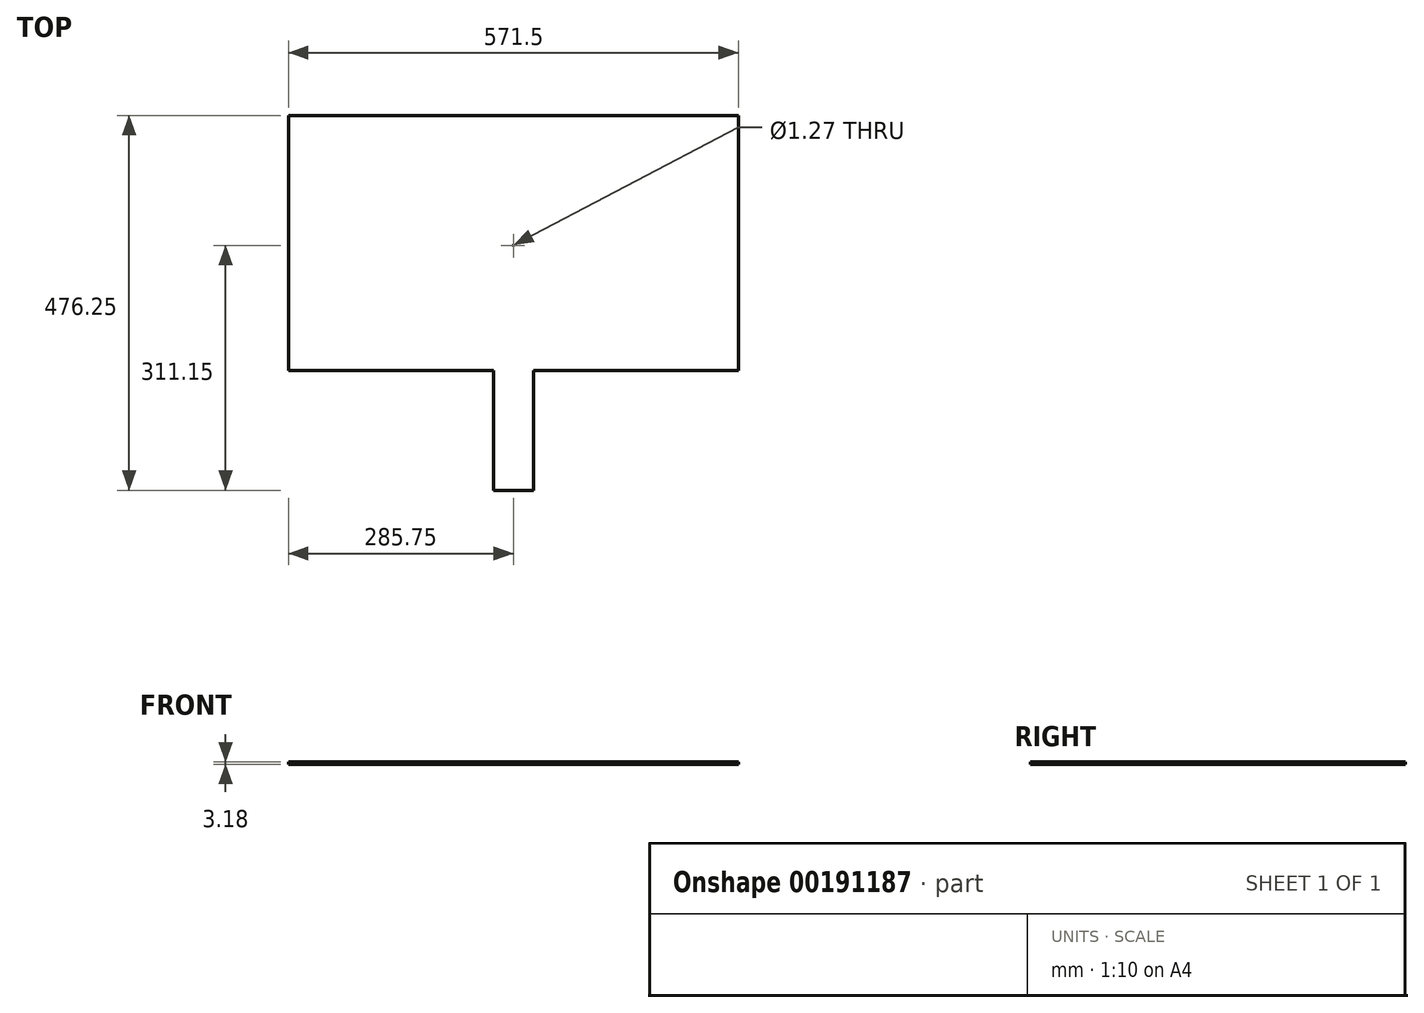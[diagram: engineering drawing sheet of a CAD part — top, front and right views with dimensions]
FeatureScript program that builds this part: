
annotation { "Feature Type Name" : "Feature", "Feature Type Description" : "" }
export const myFeature = defineFeature(function(context is Context, id is Id, definition is map)
    precondition{}
    {
        {
            var Q0;
            Q0=qCreatedBy(makeId("Top.planeOp"),FACE);
            var sketch = newSketch(context, id + "F0", { "sketchPlane" : qUnion([Q0])});
            skLineSegment(sketch, "E0", {"start": v(0, -635.05) * mm, "end": v(0, -914.35) * mm, "construction": true});
            skLineSegment(sketch, "E1.bottom", {"start": v(285.75, -298.45) * mm, "end": v(-285.75, -298.45) * mm, "construction": true});
            skLineSegment(sketch, "E1.top", {"start": v(285.75, 298.45) * mm, "end": v(-285.75, 298.45) * mm, "construction": true});
            skLineSegment(sketch, "E1.left", {"start": v(285.75, -298.45) * mm, "end": v(285.75, 298.45) * mm, "construction": true});
            skLineSegment(sketch, "E1.right", {"start": v(-285.75, -298.45) * mm, "end": v(-285.75, 298.45) * mm, "construction": true});
            skPoint(sketch, "E1.middle", {"position": v(0, 0) * mm});
            skLineSegment(sketch, "E2", {"start": v(-842.63, 0) * mm, "end": v(1673.01, 0) * mm, "construction": true});
            skPoint(sketch, "E2.endSnap0", {"position": v(285.75, 0) * mm});
            skLineSegment(sketch, "E3", {"start": v(323.85, 298.45) * mm, "end": v(323.85, -298.45) * mm, "construction": true});
            skLineSegment(sketch, "E4", {"start": v(323.85, -298.45) * mm, "end": v(577.85, -298.45) * mm});
            skLineSegment(sketch, "E5", {"start": v(577.85, -298.45) * mm, "end": v(577.85, 298.45) * mm, "construction": true});
            skLineSegment(sketch, "E6.bottom", {"start": v(-323.85, 298.45) * mm, "end": v(-577.85, 298.45) * mm});
            skLineSegment(sketch, "E6.top", {"start": v(-323.85, -298.45) * mm, "end": v(-577.85, -298.45) * mm});
            skLineSegment(sketch, "E6.left", {"start": v(-323.85, 298.45) * mm, "end": v(-323.85, -298.45) * mm, "construction": true});
            skLineSegment(sketch, "E6.right", {"start": v(-577.85, 298.45) * mm, "end": v(-577.85, -298.45) * mm});
            skLineSegment(sketch, "E7.bottom", {"start": v(285.75, 298.45) * mm, "end": v(1187.45, 298.45) * mm});
            skLineSegment(sketch, "E7.top", {"start": v(615.95, -298.45) * mm, "end": v(1187.45, -298.45) * mm});
            skLineSegment(sketch, "E7.left", {"start": v(615.95, 298.45) * mm, "end": v(615.95, -298.45) * mm, "construction": true});
            skLineSegment(sketch, "E8.bottom", {"start": v(-285.75, -336.55) * mm, "end": v(285.75, -336.55) * mm, "construction": true});
            skLineSegment(sketch, "E8.top", {"start": v(-285.75, -622.3) * mm, "end": v(-25.4, -622.3) * mm});
            skLineSegment(sketch, "E8.left", {"start": v(-285.75, -336.55) * mm, "end": v(-285.75, -622.3) * mm});
            skLineSegment(sketch, "E8.right", {"start": v(285.75, -336.55) * mm, "end": v(285.75, -622.3) * mm});
            skLineSegment(sketch, "E9.bottom", {"start": v(-285.75, 336.55) * mm, "end": v(285.75, 336.55) * mm, "construction": true});
            skLineSegment(sketch, "E9.left", {"start": v(-285.75, 336.55) * mm, "end": v(-285.75, 349.25) * mm});
            skLineSegment(sketch, "E10", {"start": v(285.75, -298.45) * mm, "end": v(323.85, -298.45) * mm});
            skLineSegment(sketch, "E11", {"start": v(577.85, -298.45) * mm, "end": v(615.95, -298.45) * mm});
            skLineSegment(sketch, "E12", {"start": v(-323.85, -298.45) * mm, "end": v(-285.75, -298.45) * mm});
            skLineSegment(sketch, "E13", {"start": v(-323.85, 298.45) * mm, "end": v(-285.75, 298.45) * mm});
            skLineSegment(sketch, "E14", {"start": v(285.75, -298.45) * mm, "end": v(285.75, -336.55) * mm});
            skLineSegment(sketch, "E15", {"start": v(-285.75, -298.45) * mm, "end": v(-285.75, -336.55) * mm});
            skLineSegment(sketch, "E16.bottom", {"start": v(1187.45, 298.45) * mm, "end": v(1276.35, 298.45) * mm});
            skLineSegment(sketch, "E16.top", {"start": v(1187.45, -298.45) * mm, "end": v(1276.35, -298.45) * mm});
            skLineSegment(sketch, "E16.left", {"start": v(1187.45, 298.45) * mm, "end": v(1187.45, -298.45) * mm, "construction": true});
            skLineSegment(sketch, "E16.right", {"start": v(1276.35, 298.45) * mm, "end": v(1276.35, -298.45) * mm});
            skLineSegment(sketch, "E17.right", {"start": v(361.95, 577.85) * mm, "end": v(361.95, 349.25) * mm});
            skLineSegment(sketch, "E18.top", {"start": v(-285.75, 298.45) * mm, "end": v(-361.95, 298.45) * mm});
            skLineSegment(sketch, "E18.left", {"start": v(-285.75, 704.85) * mm, "end": v(-285.75, 577.85) * mm});
            skLineSegment(sketch, "E18.right", {"start": v(-361.95, 577.85) * mm, "end": v(-361.95, 349.25) * mm});
            skLineSegment(sketch, "E19.top", {"start": v(-285.75, 704.85) * mm, "end": v(285.75, 704.85) * mm});
            skLineSegment(sketch, "E20", {"start": v(-361.95, 349.25) * mm, "end": v(-285.75, 349.25) * mm});
            skLineSegment(sketch, "E21", {"start": v(285.75, 349.25) * mm, "end": v(361.95, 349.25) * mm});
            skLineSegment(sketch, "E22.top", {"start": v(-25.4, -774.7) * mm, "end": v(25.4, -774.7) * mm});
            skLineSegment(sketch, "E22.left", {"start": v(25.4, -622.3) * mm, "end": v(25.4, -774.7) * mm});
            skLineSegment(sketch, "E22.right", {"start": v(-25.4, -622.3) * mm, "end": v(-25.4, -774.7) * mm});
            skLineSegment(sketch, "E23.trimOffspring", {"start": v(25.4, -622.3) * mm, "end": v(285.75, -622.3) * mm});
            skLineSegment(sketch, "E24", {"start": v(361.95, 577.85) * mm, "end": v(285.75, 577.85) * mm});
            skLineSegment(sketch, "E25", {"start": v(-361.95, 577.85) * mm, "end": v(-285.75, 577.85) * mm});
            skLineSegment(sketch, "E26", {"start": v(-285.75, 349.25) * mm, "end": v(-285.75, 298.45) * mm});
            skLineSegment(sketch, "E27", {"start": v(-285.75, 577.85) * mm, "end": v(-285.75, 349.25) * mm, "construction": true});
            skCircle(sketch, "E28", {"center": v(0, 0) * mm, "radius": 0.64 * mm});
            skPoint(sketch, "E29", {"position": v(450.85, 0) * mm});
            skPoint(sketch, "E30", {"position": v(323.85, 0) * mm});
            skPoint(sketch, "E31", {"position": v(577.85, 0) * mm});
            skPoint(sketch, "E32", {"position": v(615.95, 0) * mm});
            skPoint(sketch, "E33", {"position": v(1187.45, 0) * mm});
            skPoint(sketch, "E34", {"position": v(-323.85, 0) * mm});
            skPoint(sketch, "E35", {"position": v(-577.85, 0) * mm});
            skPoint(sketch, "E36", {"position": v(0, -336.55) * mm});
            skPoint(sketch, "E37", {"position": v(0, -590.55) * mm});
            skPoint(sketch, "E38", {"position": v(0, 349.25) * mm});
            skPoint(sketch, "E39", {"position": v(0, 577.85) * mm});
            skPoint(sketch, "E40", {"position": v(0, 463.55) * mm});
            skPoint(sketch, "E41", {"position": v(-450.85, 0) * mm});
            skPoint(sketch, "E42", {"position": v(901.7, 0) * mm});
            skPoint(sketch, "E43", {"position": v(0, -463.55) * mm});
            skCircle(sketch, "E44", {"center": v(-450.85, 0) * mm, "radius": 0.64 * mm});
            skCircle(sketch, "E45", {"center": v(450.85, 0) * mm, "radius": 0.63 * mm});
            skCircle(sketch, "E46", {"center": v(901.7, 0) * mm, "radius": 0.64 * mm});
            skCircle(sketch, "E47", {"center": v(0, -463.55) * mm, "radius": 0.63 * mm});
            skCircle(sketch, "E48", {"center": v(0, 463.55) * mm, "radius": 0.63 * mm});
            skPoint(sketch, "E49", {"position": v(0, -774.7) * mm});
            skLineSegment(sketch, "E50.trimOffspring", {"start": v(177.8, -622.3) * mm, "end": v(285.75, -622.3) * mm});
            skLineSegment(sketch, "E51", {"start": v(285.75, 704.85) * mm, "end": v(285.75, 577.85) * mm});
            skLineSegment(sketch, "E52", {"start": v(-285.75, 590.55) * mm, "end": v(285.75, 590.55) * mm, "construction": true});
            skPoint(sketch, "E53", {"position": v(990.6, 0) * mm});
            skPoint(sketch, "E54", {"position": v(812.8, 0) * mm});
            skCircle(sketch, "E55", {"center": v(812.8, 0) * mm, "radius": 0.64 * mm});
            skCircle(sketch, "E56", {"center": v(990.6, 0) * mm, "radius": 0.64 * mm});
            skLineSegment(sketch, "E57", {"start": v(-285.75, -590.55) * mm, "end": v(285.75, -590.55) * mm, "construction": true});
            skLineSegment(sketch, "E58", {"start": v(-254, -336.55) * mm, "end": v(-254, -590.55) * mm, "construction": true});
            skLineSegment(sketch, "E59.MirrorCS", {"start": v(254, -336.55) * mm, "end": v(254, -590.55) * mm, "construction": true});
            skLineSegment(sketch, "E60", {"start": v(254, -336.55) * mm, "end": v(-254, -590.55) * mm, "construction": true});
            skLineSegment(sketch, "E61", {"start": v(-254, -336.55) * mm, "end": v(254, -590.55) * mm, "construction": true});
            skLineSegment(sketch, "E62", {"start": v(285.75, 298.45) * mm, "end": v(-285.75, -298.45) * mm, "construction": true});
            skLineSegment(sketch, "E63", {"start": v(-285.75, 298.45) * mm, "end": v(285.75, -298.45) * mm, "construction": true});
            skLineSegment(sketch, "E64", {"start": v(-254, 590.55) * mm, "end": v(-254, 336.55) * mm, "construction": true});
            skLineSegment(sketch, "E65.MirrorCS", {"start": v(254, 590.55) * mm, "end": v(254, 336.55) * mm, "construction": true});
            skLineSegment(sketch, "E66", {"start": v(-254, 590.55) * mm, "end": v(254, 336.55) * mm, "construction": true});
            skLineSegment(sketch, "E67", {"start": v(-254, 336.55) * mm, "end": v(254, 590.55) * mm, "construction": true});
            skLineSegment(sketch, "E68", {"start": v(323.85, 298.45) * mm, "end": v(577.85, -298.45) * mm, "construction": true});
            skLineSegment(sketch, "E69", {"start": v(577.85, 298.45) * mm, "end": v(323.85, -298.45) * mm, "construction": true});
            skLineSegment(sketch, "E70", {"start": v(1187.45, 298.45) * mm, "end": v(615.95, -298.45) * mm, "construction": true});
            skLineSegment(sketch, "E71", {"start": v(-323.85, 298.45) * mm, "end": v(-577.85, -298.45) * mm, "construction": true});
            skLineSegment(sketch, "E72", {"start": v(-577.85, 298.45) * mm, "end": v(-323.85, -298.45) * mm, "construction": true});
            skLineSegment(sketch, "E73", {"start": v(615.95, 298.45) * mm, "end": v(1187.45, -298.45) * mm, "construction": true});
            skLineSegment(sketch, "E74", {"start": v(285.75, 298.45) * mm, "end": v(285.75, 349.25) * mm});
            skSolve(sketch);
        }
        {
            var Q0;
            Q0 = qSketchRegion(id + "F0", true);
            extrude(context, id + "F1", {"entities" : qUnion([Q0]), "depth" : 3.17 * mm});
        }
        {
            var Q0;
            Q0=makeQuery(id+"F1.opExtrude","CAP_FACE",FACE,{"disambiguationData":[OSD([sQuery(id+"F0.wireOp",EDGE,"E4"),sQuery(id+"F0.wireOp",EDGE,"mRY2fwng-EMyn-YxYV-NyzR-yqdV6J5uKH8S"),sQuery(id+"F0.wireOp",EDGE,"E6.bottom"),sQuery(id+"F0.wireOp",EDGE,"E6.top"),sQuery(id+"F0.wireOp",EDGE,"E6.right"),sQuery(id+"F0.wireOp",EDGE,"E7.bottom"),sQuery(id+"F0.wireOp",EDGE,"E7.top"),sQuery(id+"F0.wireOp",EDGE,"E8.left"),sQuery(id+"F0.wireOp",EDGE,"E8.right"),sQuery(id+"F0.wireOp",EDGE,"E10"),sQuery(id+"F0.wireOp",EDGE,"sA4iQwFo-DiBT-fMGT-JzR6-p6F9ceSemcnJ"),sQuery(id+"F0.wireOp",EDGE,"E11"),sQuery(id+"F0.wireOp",EDGE,"E12"),sQuery(id+"F0.wireOp",EDGE,"E14"),sQuery(id+"F0.wireOp",EDGE,"E15"),sQuery(id+"F0.wireOp",EDGE,"E16.bottom"),sQuery(id+"F0.wireOp",EDGE,"E16.top"),sQuery(id+"F0.wireOp",EDGE,"E16.right"),sQuery(id+"F0.wireOp",EDGE,"E17.top"),sQuery(id+"F0.wireOp",EDGE,"E17.right"),sQuery(id+"F0.wireOp",EDGE,"E18.top"),sQuery(id+"F0.wireOp",EDGE,"E18.right"),sQuery(id+"F0.wireOp",EDGE,"E19.bottom"),sQuery(id+"F0.wireOp",EDGE,"E19.top"),sQuery(id+"F0.wireOp",EDGE,"E20"),sQuery(id+"F0.wireOp",EDGE,"E21"),sQuery(id+"F0.wireOp",EDGE,"E8.top"),sQuery(id+"F0.wireOp",EDGE,"E22.top"),sQuery(id+"F0.wireOp",EDGE,"E22.left"),sQuery(id+"F0.wireOp",EDGE,"E22.right"),sQuery(id+"F0.wireOp",EDGE,"E23.trimOffspring"),sQuery(id+"F0.wireOp",EDGE,"4iudcIEB-iYir-bAQA-znhg-HSLRRKW8f51n"),sQuery(id+"F0.wireOp",EDGE,"xF0T9dwZ-jTZR-t2eK-ofbr-AFZm1iYlZQ4e"),sQuery(id+"F0.wireOp",EDGE,"E24"),sQuery(id+"F0.wireOp",EDGE,"E25"),sQuery(id+"F0.wireOp",EDGE,"73229018-e269-4e0e-8c85-239f03a1994d"),sQuery(id+"F0.wireOp",EDGE,"6cf454b5-ede0-49d4-9204-e5f682ce5569"),sQuery(id+"F0.wireOp",EDGE,"E26"),sQuery(id+"F0.wireOp",EDGE,"70cc8ee7-993e-4542-805c-fe784006b110.trimOffspring"),sQuery(id+"F0.wireOp",EDGE,"E28"),sQuery(id+"F0.wireOp",EDGE,"E44"),sQuery(id+"F0.wireOp",EDGE,"E45"),sQuery(id+"F0.wireOp",EDGE,"E46"),sQuery(id+"F0.wireOp",EDGE,"E47"),sQuery(id+"F0.wireOp",EDGE,"E48"),sQuery(id+"F0.wireOp",EDGE,"E50.trimOffspring"),sQuery(id+"F0.wireOp",EDGE,"E51")])],"isStart":false});
            var sketch = newSketch(context, id + "F2", { "sketchPlane" : qUnion([Q0])});
            skPoint(sketch, "E75", {"position": v(285.75, 628.65) * mm});
            skPoint(sketch, "E76", {"position": v(-285.75, 704.85) * mm});
            skPoint(sketch, "E77", {"position": v(0, 666.75) * mm});
            skLineSegment(sketch, "E78.bottom", {"start": v(254, 666.75) * mm, "end": v(-254, 666.75) * mm});
            skLineSegment(sketch, "E78.top", {"start": v(254, 692.15) * mm, "end": v(-254, 692.15) * mm});
            skLineSegment(sketch, "E78.left", {"start": v(254, 666.75) * mm, "end": v(254, 692.15) * mm});
            skLineSegment(sketch, "E78.right", {"start": v(-254, 666.75) * mm, "end": v(-254, 692.15) * mm});
            skPoint(sketch, "E78.middle", {"position": v(0, 679.45) * mm});
            skSolve(sketch);
        }
        {
            var Q0;
            Q0 = qSketchRegion(id + "F2", true);
            extrude(context, id + "F3", {"entities" : qUnion([Q0]), "operationType" : NewBodyOperationType.ADD, "depth" : 6.35 * mm});
        }
        {
            var Q0;
            Q0=makeQuery(id+"F1.opExtrude","CAP_FACE",FACE,{"disambiguationData":[OSD([sQuery(id+"F0.wireOp",EDGE,"E4"),sQuery(id+"F0.wireOp",EDGE,"mRY2fwng-EMyn-YxYV-NyzR-yqdV6J5uKH8S"),sQuery(id+"F0.wireOp",EDGE,"E6.bottom"),sQuery(id+"F0.wireOp",EDGE,"E6.top"),sQuery(id+"F0.wireOp",EDGE,"E6.right"),sQuery(id+"F0.wireOp",EDGE,"E7.bottom"),sQuery(id+"F0.wireOp",EDGE,"E7.top"),sQuery(id+"F0.wireOp",EDGE,"E8.left"),sQuery(id+"F0.wireOp",EDGE,"E8.right"),sQuery(id+"F0.wireOp",EDGE,"E10"),sQuery(id+"F0.wireOp",EDGE,"sA4iQwFo-DiBT-fMGT-JzR6-p6F9ceSemcnJ"),sQuery(id+"F0.wireOp",EDGE,"E11"),sQuery(id+"F0.wireOp",EDGE,"E12"),sQuery(id+"F0.wireOp",EDGE,"E14"),sQuery(id+"F0.wireOp",EDGE,"E15"),sQuery(id+"F0.wireOp",EDGE,"E16.bottom"),sQuery(id+"F0.wireOp",EDGE,"E16.top"),sQuery(id+"F0.wireOp",EDGE,"E16.right"),sQuery(id+"F0.wireOp",EDGE,"E17.top"),sQuery(id+"F0.wireOp",EDGE,"E17.right"),sQuery(id+"F0.wireOp",EDGE,"E18.top"),sQuery(id+"F0.wireOp",EDGE,"E18.right"),sQuery(id+"F0.wireOp",EDGE,"E19.bottom"),sQuery(id+"F0.wireOp",EDGE,"E19.top"),sQuery(id+"F0.wireOp",EDGE,"E20"),sQuery(id+"F0.wireOp",EDGE,"E21"),sQuery(id+"F0.wireOp",EDGE,"E8.top"),sQuery(id+"F0.wireOp",EDGE,"E22.top"),sQuery(id+"F0.wireOp",EDGE,"E22.left"),sQuery(id+"F0.wireOp",EDGE,"E22.right"),sQuery(id+"F0.wireOp",EDGE,"E23.trimOffspring"),sQuery(id+"F0.wireOp",EDGE,"4iudcIEB-iYir-bAQA-znhg-HSLRRKW8f51n"),sQuery(id+"F0.wireOp",EDGE,"xF0T9dwZ-jTZR-t2eK-ofbr-AFZm1iYlZQ4e"),sQuery(id+"F0.wireOp",EDGE,"E24"),sQuery(id+"F0.wireOp",EDGE,"E25"),sQuery(id+"F0.wireOp",EDGE,"73229018-e269-4e0e-8c85-239f03a1994d"),sQuery(id+"F0.wireOp",EDGE,"6cf454b5-ede0-49d4-9204-e5f682ce5569"),sQuery(id+"F0.wireOp",EDGE,"E26"),sQuery(id+"F0.wireOp",EDGE,"70cc8ee7-993e-4542-805c-fe784006b110.trimOffspring"),sQuery(id+"F0.wireOp",EDGE,"E28"),sQuery(id+"F0.wireOp",EDGE,"E44"),sQuery(id+"F0.wireOp",EDGE,"E45"),sQuery(id+"F0.wireOp",EDGE,"E46"),sQuery(id+"F0.wireOp",EDGE,"E47"),sQuery(id+"F0.wireOp",EDGE,"E48"),sQuery(id+"F0.wireOp",EDGE,"E50.trimOffspring"),sQuery(id+"F0.wireOp",EDGE,"E51")])],"isStart":false});
            var sketch = newSketch(context, id + "F4", { "sketchPlane" : qUnion([Q0])});
            skLineSegment(sketch, "E79.bottom", {"start": v(12.7, -711.2) * mm, "end": v(-12.7, -711.2) * mm});
            skLineSegment(sketch, "E79.top", {"start": v(12.7, -647.7) * mm, "end": v(-12.7, -647.7) * mm});
            skLineSegment(sketch, "E79.left", {"start": v(12.7, -711.2) * mm, "end": v(12.7, -647.7) * mm});
            skLineSegment(sketch, "E79.right", {"start": v(-12.7, -711.2) * mm, "end": v(-12.7, -647.7) * mm});
            skPoint(sketch, "E79.middle", {"position": v(0, -679.45) * mm});
            skPoint(sketch, "E79.middle.positionSnap0", {"position": v(0, -774.7) * mm});
            skPoint(sketch, "E79.centerSnap0", {"position": v(0, -774.7) * mm});
            skLineSegment(sketch, "E80.bottom", {"start": v(-311.15, 387.35) * mm, "end": v(-336.55, 387.35) * mm});
            skLineSegment(sketch, "E80.top", {"start": v(-311.15, 539.75) * mm, "end": v(-336.55, 539.75) * mm});
            skLineSegment(sketch, "E80.left", {"start": v(-311.15, 387.35) * mm, "end": v(-311.15, 539.75) * mm});
            skLineSegment(sketch, "E80.right", {"start": v(-336.55, 387.35) * mm, "end": v(-336.55, 539.75) * mm});
            skPoint(sketch, "E80.middle", {"position": v(-323.85, 463.55) * mm});
            skPoint(sketch, "E80.middle.positionSnap0", {"position": v(-361.95, 463.55) * mm});
            skPoint(sketch, "E80.centerSnap0", {"position": v(-361.95, 463.55) * mm});
            skLineSegment(sketch, "E81.bottom", {"start": v(336.55, 387.35) * mm, "end": v(311.15, 387.35) * mm});
            skLineSegment(sketch, "E81.top", {"start": v(336.55, 539.75) * mm, "end": v(311.15, 539.75) * mm});
            skLineSegment(sketch, "E81.left", {"start": v(336.55, 387.35) * mm, "end": v(336.55, 539.75) * mm});
            skLineSegment(sketch, "E81.right", {"start": v(311.15, 387.35) * mm, "end": v(311.15, 539.75) * mm});
            skPoint(sketch, "E81.middle", {"position": v(323.85, 463.55) * mm});
            skPoint(sketch, "E81.middle.positionSnap0", {"position": v(361.95, 463.55) * mm});
            skPoint(sketch, "E81.centerSnap0", {"position": v(361.95, 463.55) * mm});
            skSolve(sketch);
        }
        {
            var Q0;
            Q0 = qSketchRegion(id + "F4", true);
            extrude(context, id + "F5", {"entities" : qUnion([Q0]), "operationType" : NewBodyOperationType.ADD, "depth" : 6.35 * mm});
        }
        {
            var Q0;
            Q0=makeQuery(id+"F1.opExtrude","CAP_FACE",FACE,{"disambiguationData":[OSD([sQuery(id+"F0.wireOp",EDGE,"E4"),sQuery(id+"F0.wireOp",EDGE,"mRY2fwng-EMyn-YxYV-NyzR-yqdV6J5uKH8S"),sQuery(id+"F0.wireOp",EDGE,"E6.bottom"),sQuery(id+"F0.wireOp",EDGE,"E6.top"),sQuery(id+"F0.wireOp",EDGE,"E6.right"),sQuery(id+"F0.wireOp",EDGE,"E7.bottom"),sQuery(id+"F0.wireOp",EDGE,"E7.top"),sQuery(id+"F0.wireOp",EDGE,"E8.left"),sQuery(id+"F0.wireOp",EDGE,"E8.right"),sQuery(id+"F0.wireOp",EDGE,"E10"),sQuery(id+"F0.wireOp",EDGE,"sA4iQwFo-DiBT-fMGT-JzR6-p6F9ceSemcnJ"),sQuery(id+"F0.wireOp",EDGE,"E11"),sQuery(id+"F0.wireOp",EDGE,"E12"),sQuery(id+"F0.wireOp",EDGE,"E14"),sQuery(id+"F0.wireOp",EDGE,"E15"),sQuery(id+"F0.wireOp",EDGE,"E16.bottom"),sQuery(id+"F0.wireOp",EDGE,"E16.top"),sQuery(id+"F0.wireOp",EDGE,"E16.right"),sQuery(id+"F0.wireOp",EDGE,"E17.top"),sQuery(id+"F0.wireOp",EDGE,"E17.right"),sQuery(id+"F0.wireOp",EDGE,"E18.top"),sQuery(id+"F0.wireOp",EDGE,"E18.right"),sQuery(id+"F0.wireOp",EDGE,"E19.bottom"),sQuery(id+"F0.wireOp",EDGE,"E19.top"),sQuery(id+"F0.wireOp",EDGE,"E20"),sQuery(id+"F0.wireOp",EDGE,"E21"),sQuery(id+"F0.wireOp",EDGE,"E8.top"),sQuery(id+"F0.wireOp",EDGE,"E22.top"),sQuery(id+"F0.wireOp",EDGE,"E22.left"),sQuery(id+"F0.wireOp",EDGE,"E22.right"),sQuery(id+"F0.wireOp",EDGE,"E23.trimOffspring"),sQuery(id+"F0.wireOp",EDGE,"4iudcIEB-iYir-bAQA-znhg-HSLRRKW8f51n"),sQuery(id+"F0.wireOp",EDGE,"xF0T9dwZ-jTZR-t2eK-ofbr-AFZm1iYlZQ4e"),sQuery(id+"F0.wireOp",EDGE,"E24"),sQuery(id+"F0.wireOp",EDGE,"E25"),sQuery(id+"F0.wireOp",EDGE,"73229018-e269-4e0e-8c85-239f03a1994d"),sQuery(id+"F0.wireOp",EDGE,"6cf454b5-ede0-49d4-9204-e5f682ce5569"),sQuery(id+"F0.wireOp",EDGE,"E26"),sQuery(id+"F0.wireOp",EDGE,"70cc8ee7-993e-4542-805c-fe784006b110.trimOffspring"),sQuery(id+"F0.wireOp",EDGE,"E28"),sQuery(id+"F0.wireOp",EDGE,"E44"),sQuery(id+"F0.wireOp",EDGE,"E45"),sQuery(id+"F0.wireOp",EDGE,"E46"),sQuery(id+"F0.wireOp",EDGE,"E47"),sQuery(id+"F0.wireOp",EDGE,"E48"),sQuery(id+"F0.wireOp",EDGE,"E50.trimOffspring"),sQuery(id+"F0.wireOp",EDGE,"E51")])],"isStart":true});
            var sketch = newSketch(context, id + "F6", { "sketchPlane" : qUnion([Q0])});
            skPoint(sketch, "E82", {"position": v(901.7, 0) * mm});
            skLineSegment(sketch, "E83.bottom", {"start": v(1155.7, -260.35) * mm, "end": v(647.7, -260.35) * mm});
            skLineSegment(sketch, "E83.top", {"start": v(1155.7, -234.95) * mm, "end": v(647.7, -234.95) * mm});
            skLineSegment(sketch, "E83.left", {"start": v(1155.7, -260.35) * mm, "end": v(1155.7, -234.95) * mm});
            skLineSegment(sketch, "E83.right", {"start": v(647.7, -260.35) * mm, "end": v(647.7, -234.95) * mm});
            skPoint(sketch, "E83.middle", {"position": v(901.7, -247.65) * mm});
            skSolve(sketch);
        }
        {
            var Q0;
            Q0 = qSketchRegion(id + "F6", true);
            extrude(context, id + "F7", {"entities" : qUnion([Q0]), "operationType" : NewBodyOperationType.ADD, "depth" : 6.35 * mm});
        }
        {
            var Q0;
            Q0=makeQuery(id+"F1.opExtrude","CAP_FACE",FACE,{"disambiguationData":[OSD([sQuery(id+"F0.wireOp",EDGE,"E4"),sQuery(id+"F0.wireOp",EDGE,"mRY2fwng-EMyn-YxYV-NyzR-yqdV6J5uKH8S"),sQuery(id+"F0.wireOp",EDGE,"E6.bottom"),sQuery(id+"F0.wireOp",EDGE,"E6.top"),sQuery(id+"F0.wireOp",EDGE,"E6.right"),sQuery(id+"F0.wireOp",EDGE,"E7.bottom"),sQuery(id+"F0.wireOp",EDGE,"E7.top"),sQuery(id+"F0.wireOp",EDGE,"E8.left"),sQuery(id+"F0.wireOp",EDGE,"E8.right"),sQuery(id+"F0.wireOp",EDGE,"E10"),sQuery(id+"F0.wireOp",EDGE,"sA4iQwFo-DiBT-fMGT-JzR6-p6F9ceSemcnJ"),sQuery(id+"F0.wireOp",EDGE,"E11"),sQuery(id+"F0.wireOp",EDGE,"E12"),sQuery(id+"F0.wireOp",EDGE,"E14"),sQuery(id+"F0.wireOp",EDGE,"E15"),sQuery(id+"F0.wireOp",EDGE,"E16.bottom"),sQuery(id+"F0.wireOp",EDGE,"E16.top"),sQuery(id+"F0.wireOp",EDGE,"E16.right"),sQuery(id+"F0.wireOp",EDGE,"E17.top"),sQuery(id+"F0.wireOp",EDGE,"E17.right"),sQuery(id+"F0.wireOp",EDGE,"E18.top"),sQuery(id+"F0.wireOp",EDGE,"E18.right"),sQuery(id+"F0.wireOp",EDGE,"E19.bottom"),sQuery(id+"F0.wireOp",EDGE,"E19.top"),sQuery(id+"F0.wireOp",EDGE,"E20"),sQuery(id+"F0.wireOp",EDGE,"E21"),sQuery(id+"F0.wireOp",EDGE,"E8.top"),sQuery(id+"F0.wireOp",EDGE,"E22.top"),sQuery(id+"F0.wireOp",EDGE,"E22.left"),sQuery(id+"F0.wireOp",EDGE,"E22.right"),sQuery(id+"F0.wireOp",EDGE,"E23.trimOffspring"),sQuery(id+"F0.wireOp",EDGE,"4iudcIEB-iYir-bAQA-znhg-HSLRRKW8f51n"),sQuery(id+"F0.wireOp",EDGE,"xF0T9dwZ-jTZR-t2eK-ofbr-AFZm1iYlZQ4e"),sQuery(id+"F0.wireOp",EDGE,"E24"),sQuery(id+"F0.wireOp",EDGE,"E25"),sQuery(id+"F0.wireOp",EDGE,"73229018-e269-4e0e-8c85-239f03a1994d"),sQuery(id+"F0.wireOp",EDGE,"6cf454b5-ede0-49d4-9204-e5f682ce5569"),sQuery(id+"F0.wireOp",EDGE,"E26"),sQuery(id+"F0.wireOp",EDGE,"70cc8ee7-993e-4542-805c-fe784006b110.trimOffspring"),sQuery(id+"F0.wireOp",EDGE,"E28"),sQuery(id+"F0.wireOp",EDGE,"E44"),sQuery(id+"F0.wireOp",EDGE,"E45"),sQuery(id+"F0.wireOp",EDGE,"E46"),sQuery(id+"F0.wireOp",EDGE,"E47"),sQuery(id+"F0.wireOp",EDGE,"E48"),sQuery(id+"F0.wireOp",EDGE,"E50.trimOffspring"),sQuery(id+"F0.wireOp",EDGE,"E51")])],"isStart":true});
            var sketch = newSketch(context, id + "F8", { "sketchPlane" : qUnion([Q0])});
            skPoint(sketch, "E84", {"position": v(311.15, -387.35) * mm});
            skPoint(sketch, "E85", {"position": v(285.75, -298.45) * mm});
            skLineSegment(sketch, "E86.bottom", {"start": v(527.05, -273.05) * mm, "end": v(374.65, -273.05) * mm});
            skLineSegment(sketch, "E86.top", {"start": v(527.05, -247.65) * mm, "end": v(374.65, -247.65) * mm});
            skLineSegment(sketch, "E86.left", {"start": v(527.05, -273.05) * mm, "end": v(527.05, -247.65) * mm});
            skLineSegment(sketch, "E86.right", {"start": v(374.65, -273.05) * mm, "end": v(374.65, -247.65) * mm});
            skPoint(sketch, "E86.middle", {"position": v(450.85, -260.35) * mm});
            skLineSegment(sketch, "E87.MirrorCS", {"start": v(-374.65, -273.05) * mm, "end": v(-374.65, -247.65) * mm});
            skLineSegment(sketch, "E88.MirrorCS", {"start": v(-527.05, -273.05) * mm, "end": v(-374.65, -273.05) * mm});
            skLineSegment(sketch, "E89.MirrorCS", {"start": v(-527.05, -247.65) * mm, "end": v(-374.65, -247.65) * mm});
            skLineSegment(sketch, "E90.MirrorCS", {"start": v(-527.05, -273.05) * mm, "end": v(-527.05, -247.65) * mm});
            skSolve(sketch);
        }
        {
            var Q0;
            Q0 = qSketchRegion(id + "F8", true);
            extrude(context, id + "F9", {"entities" : qUnion([Q0]), "operationType" : NewBodyOperationType.ADD, "depth" : 6.35 * mm});
        }
        {
            var Q0;
            Q0=makeQuery(id+"F1.opExtrude","CAP_FACE",FACE,{"disambiguationData":[OSD([sQuery(id+"F0.wireOp",EDGE,"E4"),sQuery(id+"F0.wireOp",EDGE,"mRY2fwng-EMyn-YxYV-NyzR-yqdV6J5uKH8S"),sQuery(id+"F0.wireOp",EDGE,"E6.bottom"),sQuery(id+"F0.wireOp",EDGE,"E6.top"),sQuery(id+"F0.wireOp",EDGE,"E6.right"),sQuery(id+"F0.wireOp",EDGE,"E7.bottom"),sQuery(id+"F0.wireOp",EDGE,"E7.top"),sQuery(id+"F0.wireOp",EDGE,"E8.left"),sQuery(id+"F0.wireOp",EDGE,"E8.right"),sQuery(id+"F0.wireOp",EDGE,"E10"),sQuery(id+"F0.wireOp",EDGE,"sA4iQwFo-DiBT-fMGT-JzR6-p6F9ceSemcnJ"),sQuery(id+"F0.wireOp",EDGE,"E11"),sQuery(id+"F0.wireOp",EDGE,"E12"),sQuery(id+"F0.wireOp",EDGE,"E14"),sQuery(id+"F0.wireOp",EDGE,"E15"),sQuery(id+"F0.wireOp",EDGE,"E16.bottom"),sQuery(id+"F0.wireOp",EDGE,"E16.top"),sQuery(id+"F0.wireOp",EDGE,"E16.right"),sQuery(id+"F0.wireOp",EDGE,"E17.top"),sQuery(id+"F0.wireOp",EDGE,"E17.right"),sQuery(id+"F0.wireOp",EDGE,"E18.top"),sQuery(id+"F0.wireOp",EDGE,"E18.right"),sQuery(id+"F0.wireOp",EDGE,"E19.bottom"),sQuery(id+"F0.wireOp",EDGE,"E19.top"),sQuery(id+"F0.wireOp",EDGE,"E20"),sQuery(id+"F0.wireOp",EDGE,"E21"),sQuery(id+"F0.wireOp",EDGE,"E8.top"),sQuery(id+"F0.wireOp",EDGE,"E22.top"),sQuery(id+"F0.wireOp",EDGE,"E22.left"),sQuery(id+"F0.wireOp",EDGE,"E22.right"),sQuery(id+"F0.wireOp",EDGE,"E23.trimOffspring"),sQuery(id+"F0.wireOp",EDGE,"4iudcIEB-iYir-bAQA-znhg-HSLRRKW8f51n"),sQuery(id+"F0.wireOp",EDGE,"xF0T9dwZ-jTZR-t2eK-ofbr-AFZm1iYlZQ4e"),sQuery(id+"F0.wireOp",EDGE,"E24"),sQuery(id+"F0.wireOp",EDGE,"E25"),sQuery(id+"F0.wireOp",EDGE,"73229018-e269-4e0e-8c85-239f03a1994d"),sQuery(id+"F0.wireOp",EDGE,"6cf454b5-ede0-49d4-9204-e5f682ce5569"),sQuery(id+"F0.wireOp",EDGE,"E26"),sQuery(id+"F0.wireOp",EDGE,"70cc8ee7-993e-4542-805c-fe784006b110.trimOffspring"),sQuery(id+"F0.wireOp",EDGE,"E28"),sQuery(id+"F0.wireOp",EDGE,"E44"),sQuery(id+"F0.wireOp",EDGE,"E45"),sQuery(id+"F0.wireOp",EDGE,"E46"),sQuery(id+"F0.wireOp",EDGE,"E47"),sQuery(id+"F0.wireOp",EDGE,"E48"),sQuery(id+"F0.wireOp",EDGE,"E50.trimOffspring"),sQuery(id+"F0.wireOp",EDGE,"E51")])],"isStart":false});
            var sketch = newSketch(context, id + "F10", { "sketchPlane" : qUnion([Q0])});
            skLineSegment(sketch, "E91.bottom", {"start": v(1263.65, 76.2) * mm, "end": v(1238.25, 76.2) * mm});
            skLineSegment(sketch, "E91.top", {"start": v(1263.65, 228.6) * mm, "end": v(1238.25, 228.6) * mm});
            skLineSegment(sketch, "E91.left", {"start": v(1263.65, 76.2) * mm, "end": v(1263.65, 228.6) * mm});
            skLineSegment(sketch, "E91.right", {"start": v(1238.25, 76.2) * mm, "end": v(1238.25, 228.6) * mm});
            skPoint(sketch, "E91.middle", {"position": v(1250.95, 152.4) * mm});
            skLineSegment(sketch, "E92.MirrorCS", {"start": v(1263.65, -76.2) * mm, "end": v(1238.25, -76.2) * mm});
            skLineSegment(sketch, "E93.MirrorCS", {"start": v(1263.65, -76.2) * mm, "end": v(1263.65, -228.6) * mm});
            skLineSegment(sketch, "E94.MirrorCS", {"start": v(1238.25, -76.2) * mm, "end": v(1238.25, -228.6) * mm});
            skLineSegment(sketch, "E95.MirrorCS", {"start": v(1263.65, -228.6) * mm, "end": v(1238.25, -228.6) * mm});
            skSolve(sketch);
        }
        {
            var Q0;
            Q0 = qSketchRegion(id + "F10", true);
            extrude(context, id + "F11", {"entities" : qUnion([Q0]), "operationType" : NewBodyOperationType.ADD, "depth" : 6.35 * mm});
        }
        {
            var Q0;
            Q0=makeQuery(id+"F0.imprint","IMPRINT",FACE,{"disambiguationData":[TD([[makeQuery(id+"F0.imprint","IMPRINT",EDGE,{"derivedFrom":sQuery(id+"F0.wireOp",EDGE,"E4")}),1.0]])]});
            var sketch = newSketch(context, id + "F12", { "sketchPlane" : qUnion([Q0])});
            skLineSegment(sketch, "E96.bottom", {"start": v(-565.15, 76.2) * mm, "end": v(-539.75, 76.2) * mm});
            skLineSegment(sketch, "E96.top", {"start": v(-565.15, 228.6) * mm, "end": v(-539.75, 228.6) * mm});
            skLineSegment(sketch, "E96.left", {"start": v(-565.15, 76.2) * mm, "end": v(-565.15, 228.6) * mm});
            skLineSegment(sketch, "E96.right", {"start": v(-539.75, 76.2) * mm, "end": v(-539.75, 228.6) * mm});
            skPoint(sketch, "E96.middle", {"position": v(-552.45, 152.4) * mm});
            skLineSegment(sketch, "E97.MirrorCS", {"start": v(-539.75, -76.2) * mm, "end": v(-539.75, -228.6) * mm});
            skLineSegment(sketch, "E98.MirrorCS", {"start": v(-565.15, -228.6) * mm, "end": v(-539.75, -228.6) * mm});
            skLineSegment(sketch, "E99.MirrorCS", {"start": v(-565.15, -76.2) * mm, "end": v(-565.15, -228.6) * mm});
            skLineSegment(sketch, "E100.MirrorCS", {"start": v(-565.15, -76.2) * mm, "end": v(-539.75, -76.2) * mm});
            skSolve(sketch);
        }
        {
            var Q0;
            Q0 = qSketchRegion(id + "F12", true);
            extrude(context, id + "F13", {"entities" : qUnion([Q0]), "operationType" : NewBodyOperationType.ADD, "oppositeDirection" : true, "depth" : 6.35 * mm});
        }
        {
            var Q0;
            Q0=makeQuery(id+"F1.opExtrude","CAP_FACE",FACE,{"disambiguationData":[OSD([sQuery(id+"F0.wireOp",EDGE,"E4"),sQuery(id+"F0.wireOp",EDGE,"mRY2fwng-EMyn-YxYV-NyzR-yqdV6J5uKH8S"),sQuery(id+"F0.wireOp",EDGE,"E6.bottom"),sQuery(id+"F0.wireOp",EDGE,"E6.top"),sQuery(id+"F0.wireOp",EDGE,"E6.right"),sQuery(id+"F0.wireOp",EDGE,"E7.bottom"),sQuery(id+"F0.wireOp",EDGE,"E7.top"),sQuery(id+"F0.wireOp",EDGE,"E8.left"),sQuery(id+"F0.wireOp",EDGE,"E8.right"),sQuery(id+"F0.wireOp",EDGE,"E10"),sQuery(id+"F0.wireOp",EDGE,"sA4iQwFo-DiBT-fMGT-JzR6-p6F9ceSemcnJ"),sQuery(id+"F0.wireOp",EDGE,"E11"),sQuery(id+"F0.wireOp",EDGE,"E12"),sQuery(id+"F0.wireOp",EDGE,"E14"),sQuery(id+"F0.wireOp",EDGE,"E15"),sQuery(id+"F0.wireOp",EDGE,"E16.bottom"),sQuery(id+"F0.wireOp",EDGE,"E16.top"),sQuery(id+"F0.wireOp",EDGE,"E16.right"),sQuery(id+"F0.wireOp",EDGE,"E17.top"),sQuery(id+"F0.wireOp",EDGE,"E17.right"),sQuery(id+"F0.wireOp",EDGE,"E18.top"),sQuery(id+"F0.wireOp",EDGE,"E18.right"),sQuery(id+"F0.wireOp",EDGE,"E19.bottom"),sQuery(id+"F0.wireOp",EDGE,"E19.top"),sQuery(id+"F0.wireOp",EDGE,"E20"),sQuery(id+"F0.wireOp",EDGE,"E21"),sQuery(id+"F0.wireOp",EDGE,"E8.top"),sQuery(id+"F0.wireOp",EDGE,"E22.top"),sQuery(id+"F0.wireOp",EDGE,"E22.left"),sQuery(id+"F0.wireOp",EDGE,"E22.right"),sQuery(id+"F0.wireOp",EDGE,"E23.trimOffspring"),sQuery(id+"F0.wireOp",EDGE,"4iudcIEB-iYir-bAQA-znhg-HSLRRKW8f51n"),sQuery(id+"F0.wireOp",EDGE,"xF0T9dwZ-jTZR-t2eK-ofbr-AFZm1iYlZQ4e"),sQuery(id+"F0.wireOp",EDGE,"E24"),sQuery(id+"F0.wireOp",EDGE,"E25"),sQuery(id+"F0.wireOp",EDGE,"73229018-e269-4e0e-8c85-239f03a1994d"),sQuery(id+"F0.wireOp",EDGE,"6cf454b5-ede0-49d4-9204-e5f682ce5569"),sQuery(id+"F0.wireOp",EDGE,"E26"),sQuery(id+"F0.wireOp",EDGE,"70cc8ee7-993e-4542-805c-fe784006b110.trimOffspring"),sQuery(id+"F0.wireOp",EDGE,"E28"),sQuery(id+"F0.wireOp",EDGE,"E44"),sQuery(id+"F0.wireOp",EDGE,"E45"),sQuery(id+"F0.wireOp",EDGE,"E46"),sQuery(id+"F0.wireOp",EDGE,"E47"),sQuery(id+"F0.wireOp",EDGE,"E48"),sQuery(id+"F0.wireOp",EDGE,"E50.trimOffspring"),sQuery(id+"F0.wireOp",EDGE,"E51"),sQuery(id+"F0.wireOp",EDGE,"E55"),sQuery(id+"F0.wireOp",EDGE,"E56")])],"isStart":true});
            var sketch = newSketch(context, id + "F14", { "sketchPlane" : qUnion([Q0])});
            skLineSegment(sketch, "E101.bottom", {"start": v(939.8, 234.95) * mm, "end": v(863.6, 234.95) * mm});
            skLineSegment(sketch, "E101.top", {"start": v(939.8, 260.35) * mm, "end": v(863.6, 260.35) * mm});
            skLineSegment(sketch, "E101.left", {"start": v(939.8, 234.95) * mm, "end": v(939.8, 260.35) * mm});
            skLineSegment(sketch, "E101.right", {"start": v(863.6, 234.95) * mm, "end": v(863.6, 260.35) * mm});
            skSolve(sketch);
        }
        {
            var Q0;
            Q0 = qSketchRegion(id + "F14", true);
            extrude(context, id + "F15", {"entities" : qUnion([Q0]), "operationType" : NewBodyOperationType.ADD, "depth" : 6.35 * mm});
        }
        {
            var Q0;
            Q0=makeQuery(id+"F1.opExtrude","SWEPT_FACE",FACE,{"disambiguationData":[OSD([sQuery(id+"F0.wireOp",EDGE,"E4"),sQuery(id+"F0.wireOp",EDGE,"E7.top"),sQuery(id+"F0.wireOp",EDGE,"E10"),sQuery(id+"F0.wireOp",EDGE,"E11"),sQuery(id+"F0.wireOp",EDGE,"E16.top")])]});
            var sketch = newSketch(context, id + "F16", { "sketchPlane" : qUnion([Q0])});
            skLineSegment(sketch, "E102.bottom", {"start": v(285.75, 0) * mm, "end": v(-285.75, 0) * mm});
            skLineSegment(sketch, "E102.top", {"start": v(285.75, 3.18) * mm, "end": v(-285.75, 3.17) * mm});
            skLineSegment(sketch, "E102.left", {"start": v(285.75, 0) * mm, "end": v(285.75, 3.18) * mm});
            skLineSegment(sketch, "E102.right", {"start": v(-285.75, 0) * mm, "end": v(-285.75, 3.17) * mm});
            skSolve(sketch);
        }
        {
            var Q0;
            Q0 = qSketchRegion(id + "F16", true);
            extrude(context, id + "F17", {"entities" : qUnion([Q0]), "operationType" : NewBodyOperationType.INTERSECT, "endBound" : BoundingType.THROUGH_ALL, "depth" : 25.4 * mm});
        }
    });
